# Revit family: 44160210(2023)
name_source: partatom
category: Plumbing Fixtures
units: mm (PartAtom-declared; Revit-internal decimal feet)

## family parameters
Always vertical = Yes
Cut with Voids When Loaded = No
OmniClass Number = 23.45.55.00
OmniClass Title = Sanitary Faucets, Wastes
Part Type = Normal
Room Calculation Point = No
Round Connector Dimension = Use Diameter
Shared = No
Work Plane-Based = No

## types (3) — shared parameters
2D/3D/BIM Files URL = http://static.hansa.com
3D View = https://static.hansa.com
Advanced Features = Flexible length / can be shortened;Hose guide, revolving
AssetType = Fixed
BodyMaterial = Brass
Brand = HANSA
Catalog Drawing URL = http://static.hansa.com
Dimension Drawing URL = http://static.hansa.com
DurationUnit = Year
EN Standard = EN1112
ETIM Class Number = EC010109 Sliding rod combination
FDV Document URL = http://www.hansa.com
Finish = Polished
Flow Drawing URL = http://static.hansa.com
Flow Rate At 300kPa With Flow Controller = 0.2 L/s
Group = Shower set
Hand Shower Size = Ø110
IfcExportAs = IfcValveType
IfcExportType = FAUCET
Installation Type = Wall mounted
Installation and Maintenance Guide URL = http://static.hansa.com
Interactive AR View URL = https://static.hansa.com
Manufacturer = HANSA
ManufacturerName = HANSA
ManufacturerURL = http://www.hansa.com
Market = Austria;Belgium;Czech Republic;Germany;Spain;France;International;Italy;Netherlands;Slovakia
Material = Brass/Plastic
Max. Hot Water Supply = 65 °C
Mobile Product Information URL = http://mpi.hansa.com
NBSDescription = Shower mixers
NBSReference = 45-35-70/335
Noise Class = I (ISO 3822)
NominalDepth = 124 mm  [stored 0.406824 ft]
NominalHeight = 765 mm
NominalWidth = 237 mm
Product Family = HANSAVIVA
Product Image URL = http://static.hansa.com
Product URL = http://static.hansa.com
Sales Package dimensions (LxWxH) = 779 x 156 x 74
Shape = Sculptured
Shower Spray = Normal;Massage;Rain
Shower Spray Number = 3 shower sprays
Size = 240x125x765 mm
Technical DataSheet URL = http://www.hansa.com
UNSPSC Class Number = 30181503 Showers
URL Declaration Of Performance (DOP) = http://static.hansa.com
URL Declaration of Asbestos = http://static.hansa.com
URL Declaration of Conformity = http://static.hansa.com
URL Declaration of SCIP = http://static.hansa.com
URL EU Packaging Declaration = http://static.hansa.com
URL EcoLabel Declaration = http://static.hansa.com
URL REACH = http://static.hansa.com
URL UWL = http://static.hansa.com
Uniclass2 = Pr_40_30_96_78
Uniclass2015Description = Shower manual water supply sets
Uniclass2015Reference = Pr_40_20_87_78
Version = 1
VersionDate = 20/04/2024
Warranty Information URL = http://warranty.hansa.com
WarrantyDescription = http://warranty.hansa.com
WarrantyDurationUnit = Year
Working Pressure = 50 - 500 kPa
zero-valued in all types: CloseOffRating, Default Elevation, FlowCoefficient

## per-type parameters (varying)
| type | BIMObjectName | Color | EAN Number | FaucetMainMaterial | ModelReference | Product Code | Shower Parts | Surface treatment | Type | URL Materials Declaration |
| 44160210 Shower set | 44160210(2023) | Chrome | 4057304013041 | Chrome | 44160210 | 44160210 | Hand shower;Shower rail;Adjustable shower rail bracket;Soap dish;Shower hose (1250 mm);Variable fixing points;Anti limescale technology (easy to clean);Twist guard for shower hose | Chrome | 0 |  |
| 4416021080 Shower set | 4416021080(2024) | Brushed steel | 4057304022005 | Brushed Steel | 4416021080 | 4416021080 | Hand shower;Shower rail;Variable fixing points;Adjustable shower rail bracket;Soap dish;Anti limescale technology (easy to clean);Shower hose (1750 mm);Twist guard for shower hose | Brushed steel | 80 | http://www.hansa.com |
| 4416021081 Shower set | 4416021081(2024) | BrushedBronze | 4057304022012 | Brushed Bronze | 4416021081 | 4416021081 | Hand shower;Shower rail;Variable fixing points;Adjustable shower rail bracket;Soap dish;Anti limescale technology (easy to clean);Shower hose (1750 mm);Twist guard for shower hose | BrushedBronze | 81 | http://www.hansa.com |

note: column(s) folded — value = type name in every type: Model, Name, Name_en

note: [stored X ft] marks values corroborated as IEEE doubles in the binary element streams (Revit-internal decimal feet)

## geometry (parser evidence)
native form markers: Sweep x5
no freeform markers — native parametric forms only
